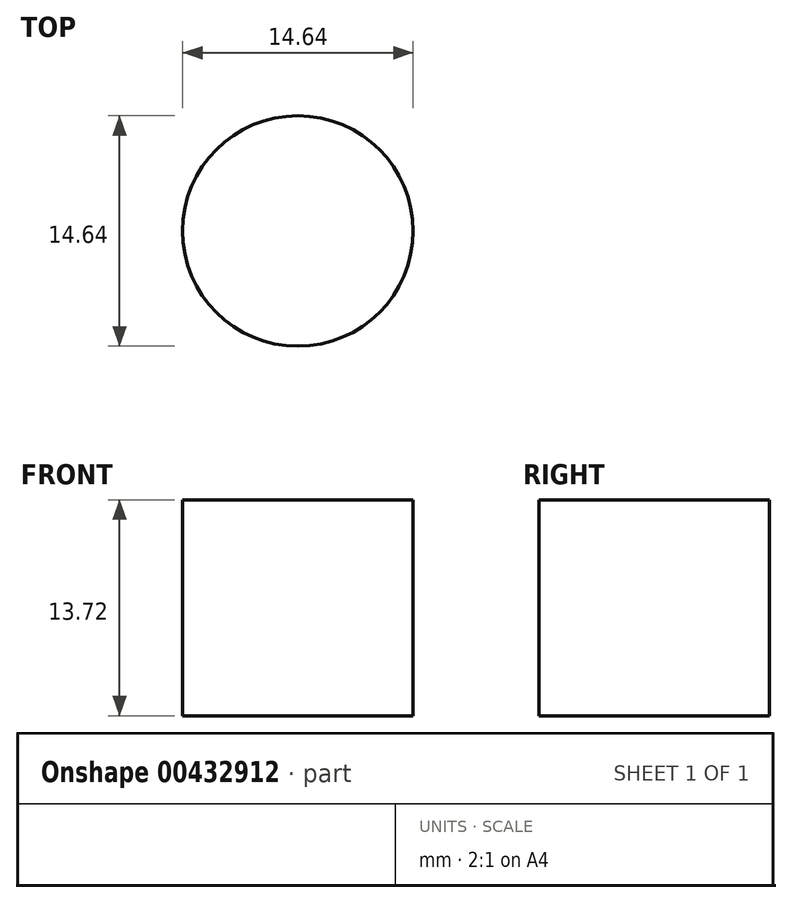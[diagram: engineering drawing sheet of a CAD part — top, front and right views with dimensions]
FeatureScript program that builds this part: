
annotation { "Feature Type Name" : "Feature", "Feature Type Description" : "" }
export const myFeature = defineFeature(function(context is Context, id is Id, definition is map)
    precondition{}
    {
        {
            var Q0;
            Q0=qCreatedBy(makeId("Top.planeOp"),FACE);
            var sketch = newSketch(context, id + "F0", { "sketchPlane" : qUnion([Q0])});
            skCircle(sketch, "E0", {"center": v(-37.17, 2.55) * mm, "radius": 7.32 * mm});
            skSolve(sketch);
        }
        {
            var Q0;
            Q0 = qSketchRegion(id + "F0", true);
            var Q1;
            Q1=makeQuery(id+"F0.imprint","IMPRINT",FACE,{"disambiguationData":[TD([[makeQuery(id+"F0.imprint","IMPRINT",EDGE,{"derivedFrom":sQuery(id+"F0.wireOp",EDGE,"E0")}),1.0]])]});
            extrude(context, id + "F1", {"entities" : qUnion([Q0, Q1]), "depth" : 13.72 * mm});
        }
    });
